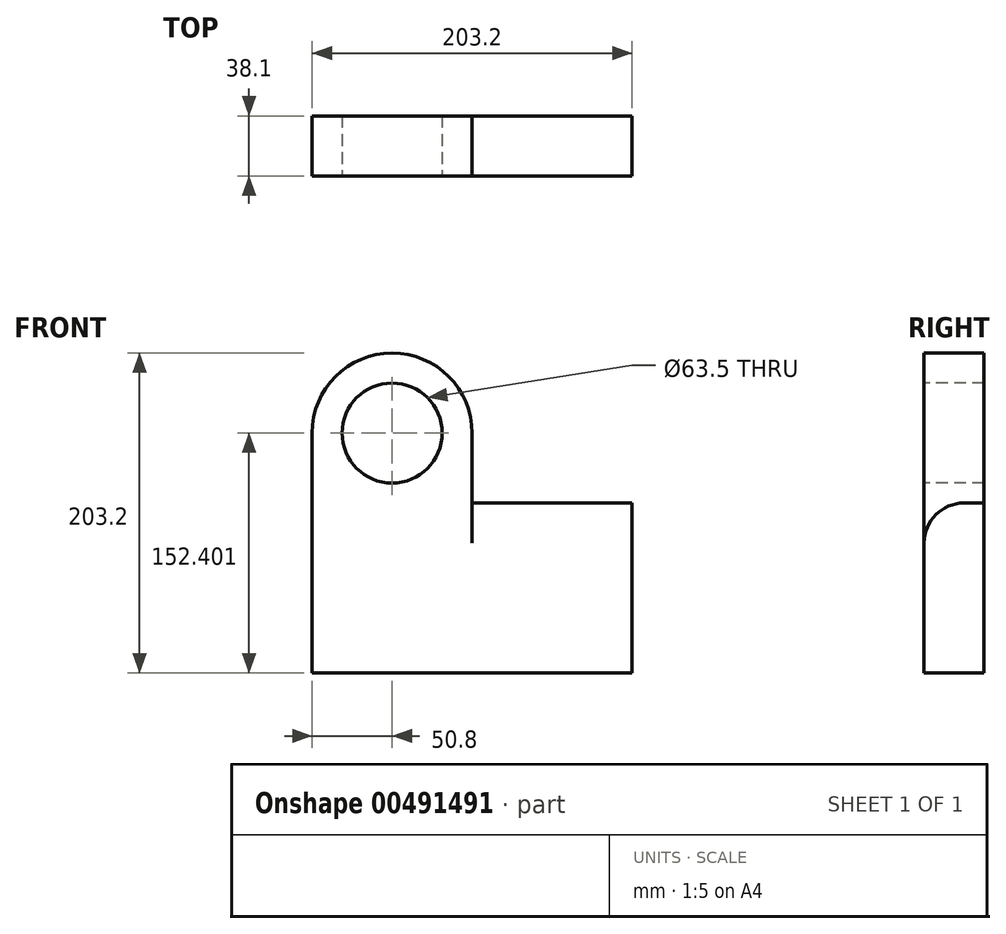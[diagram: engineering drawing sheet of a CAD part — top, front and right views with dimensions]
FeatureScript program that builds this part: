
annotation { "Feature Type Name" : "Feature", "Feature Type Description" : "" }
export const myFeature = defineFeature(function(context is Context, id is Id, definition is map)
    precondition{}
    {
        {
            var Q0;
            Q0=qCreatedBy(makeId("Front.planeOp"),FACE);
            var sketch = newSketch(context, id + "F0", { "sketchPlane" : qUnion([Q0])});
            skLineSegment(sketch, "E0", {"start": v(-129.2, 62.4) * mm, "end": v(-129.2, -90) * mm});
            skLineSegment(sketch, "E1", {"start": v(-129.2, -90) * mm, "end": v(74, -90) * mm});
            skLineSegment(sketch, "E2", {"start": v(74, -90) * mm, "end": v(74, 17.94) * mm});
            skArc(sketch, "E3", {"start": v(-27.6, 62.4) * mm, "mid": v(-78.4, 113.2) * mm, "end": v(-129.2, 62.4) * mm});
            skLineSegment(sketch, "E4", {"start": v(-27.6, 62.4) * mm, "end": v(-27.6, 17.94) * mm});
            skLineSegment(sketch, "E5", {"start": v(-27.6, 17.94) * mm, "end": v(74, 17.94) * mm});
            skSolve(sketch);
        }
        {
            var Q0;
            Q0=makeQuery(id+"F0.imprint","IMPRINT",FACE,{"disambiguationData":[TD([[makeQuery(id+"F0.imprint","IMPRINT",EDGE,{"derivedFrom":sQuery(id+"F0.wireOp",EDGE,"E0")}),1.0]])]});
            extrude(context, id + "F1", {"entities" : qUnion([Q0]), "depth" : 38.1 * mm});
        }
        {
            var Q0;
            Q0=makeQuery(id+"F1.opExtrude","CAP_EDGE",EDGE,{"disambiguationData":[OSD([sQuery(id+"F0.wireOp",EDGE,"E5")])],"isStart":false});
            fillet(context, id + "F2", {"entities" : qUnion([Q0]), "radius" : 25.4 * mm, "tangentPropagation" : true, "allowEdgeOverflow" : false});
        }
        {
            var Q0;
            Q0=makeQuery(id+"F1.opExtrude","CAP_FACE",FACE,{"disambiguationData":[OSD([sQuery(id+"F0.wireOp",EDGE,"E0"),sQuery(id+"F0.wireOp",EDGE,"E1"),sQuery(id+"F0.wireOp",EDGE,"E2"),sQuery(id+"F0.wireOp",EDGE,"E3"),sQuery(id+"F0.wireOp",EDGE,"E4"),sQuery(id+"F0.wireOp",EDGE,"E5")])],"isStart":false});
            var sketch = newSketch(context, id + "F3", { "sketchPlane" : qUnion([Q0])});
            skCircle(sketch, "E6", {"center": v(-78.4, 62.4) * mm, "radius": 31.75 * mm});
            skSolve(sketch);
        }
        {
            var Q0;
            Q0=qSketchRegion(id+"F3",true);
            extrude(context, id + "F4", {"entities" : qUnion([Q0]), "operationType" : NewBodyOperationType.REMOVE, "oppositeDirection" : true, "depth" : 50.8 * mm});
        }
    });
